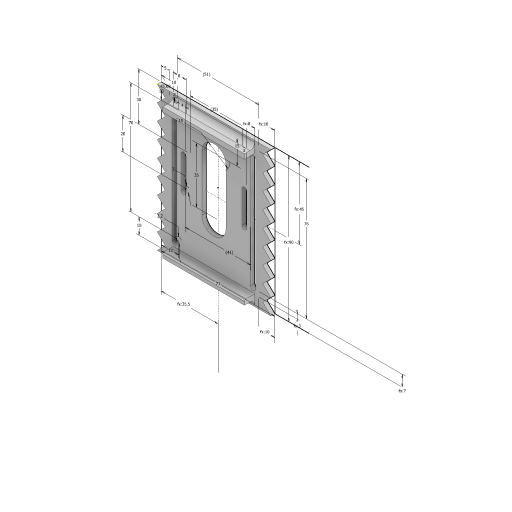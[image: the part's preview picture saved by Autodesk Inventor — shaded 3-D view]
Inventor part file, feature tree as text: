
AUTODESK INVENTOR PART (.ipt)
format: ipt  version: 2023 (Build 270158000, 158)  size: 255,488 bytes
history: native  units: mm
features: extrude x3, fillet x3, sketch x2, other x2
ambient origin geometry x8: Origin, YZ Plane, XZ Plane, XY Plane, X Axis, Y Axis, Z Axis, Center Point
bodies: Solid1 (feature_tree)
feature tree (10):
  sketch  "Sketch1"  dims[d0=71.0mm d1=90.0mm]
  extrude  "Extrusion1"  Depth=90.0mm
  extrude  "Extrusion2"  Depth=1.0mm
  fillet  "Fillet1"  Radius=10.0mm
  extrude  "Extrusion3"  Depth=1.0mm
  sketch  "Sketch2"  dims[d2=45.0deg d3=5.0mm d4=90.0mm d6=10.0mm d7=10.0mm d9=10.0mm d11=35.5mm d12=10.0mm d13=10.0mm d14=3.0mm d15=10.0mm d16=3.0mm d17=76.0mm d19=7.0mm d20=3.2mm d21=11.0mm d22=10.0mm d24=51.0mm d25=3.0mm d26=4.0mm d27=30.0mm d28=20.0mm d29=35.0mm d30=41.0mm d31=2.5mm d32=0.0mm d33=9.0mm d34=0.0mm d35=3.0mm d39=35.0mm d40=15.0mm d41=15.0mm d42=0.0mm d43=0.0mm d44=70.0mm d45=45.0mm d48=3.0mm d49=8.0mm d50=8.0mm d51=0.0mm d52=0.0mm d53=3.0mm d54=2.0mm d55=3.0mm d56=8.0mm d57=1.0mm]
  other  "Work Point1"
  other  "Work Point2"
  fillet  "Fillet2"  Radius=10.0mm
  fillet  "Fillet3"  Radius=10.0mm
